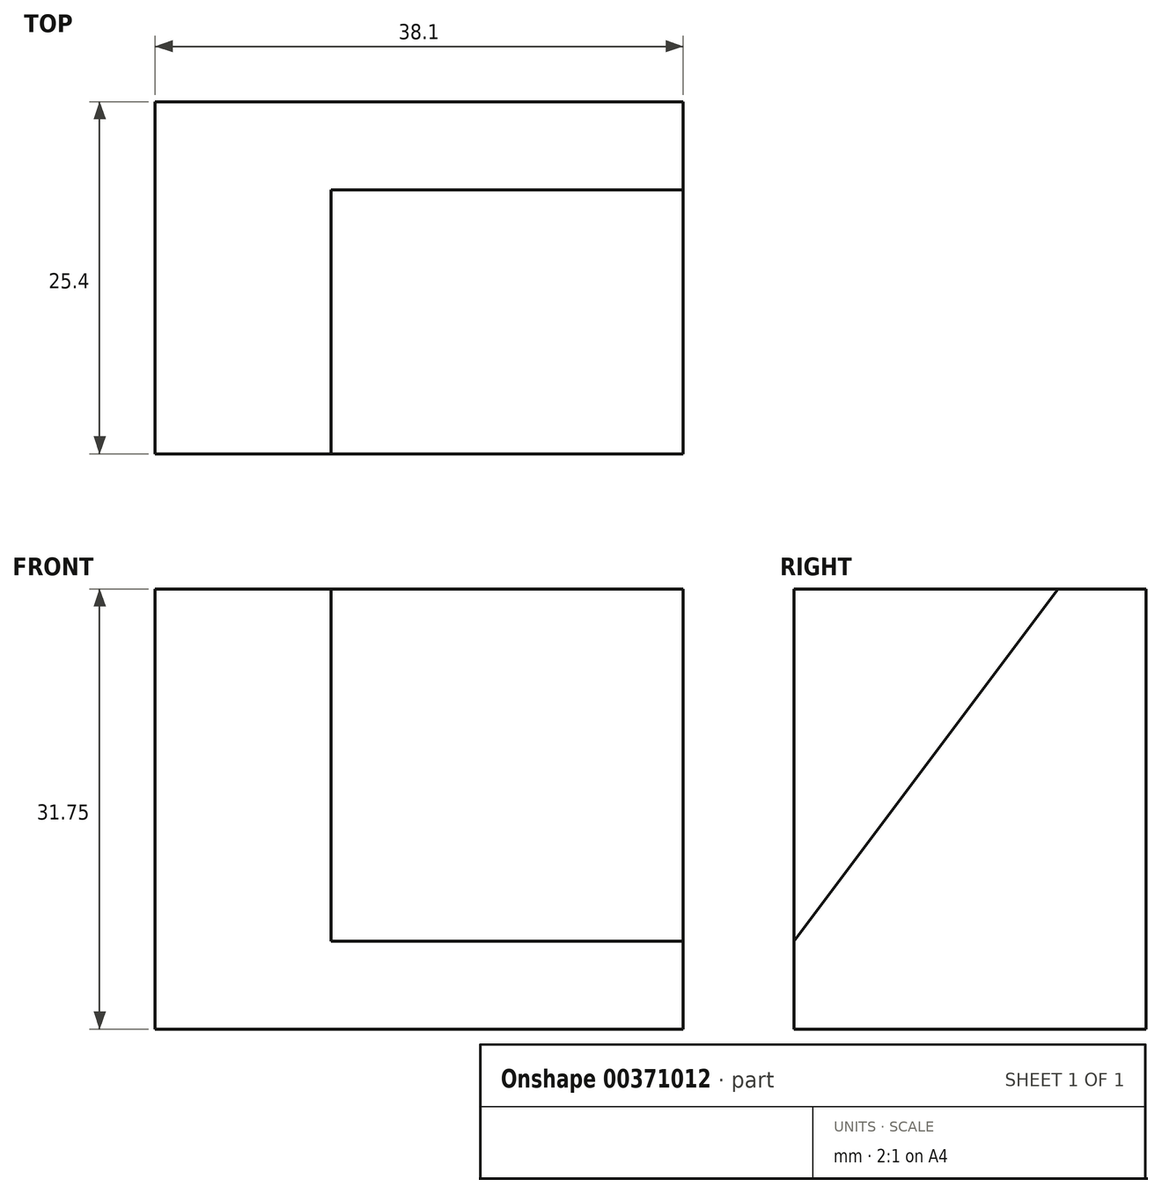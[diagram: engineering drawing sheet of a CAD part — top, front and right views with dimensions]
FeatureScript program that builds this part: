
annotation { "Feature Type Name" : "Feature", "Feature Type Description" : "" }
export const myFeature = defineFeature(function(context is Context, id is Id, definition is map)
    precondition{}
    {
        {
            var Q0;
            Q0=qCreatedBy(makeId("Top.planeOp"),FACE);
            var sketch = newSketch(context, id + "F0", { "sketchPlane" : qUnion([Q0])});
            skLineSegment(sketch, "E0", {"start": v(0, 0) * mm, "end": v(38.1, 0) * mm});
            skLineSegment(sketch, "E1", {"start": v(38.1, 0) * mm, "end": v(38.1, 25.4) * mm});
            skLineSegment(sketch, "E2", {"start": v(38.1, 25.4) * mm, "end": v(0, 25.4) * mm});
            skLineSegment(sketch, "E3", {"start": v(0, 25.4) * mm, "end": v(0, 0) * mm});
            skSolve(sketch);
        }
        {
            var Q0;
            Q0=makeQuery(id+"F0.imprint","IMPRINT",FACE,{"disambiguationData":[TD([[makeQuery(id+"F0.imprint","IMPRINT",EDGE,{"derivedFrom":sQuery(id+"F0.wireOp",EDGE,"E0")}),1.0]])]});
            extrude(context, id + "F1", {"entities" : qUnion([Q0]), "depth" : 31.75 * mm});
        }
        {
            var Q0;
            Q0=makeQuery(id+"F1.opExtrude","SWEPT_FACE",FACE,{"disambiguationData":[OSD([sQuery(id+"F0.wireOp",EDGE,"E1")])]});
            var sketch = newSketch(context, id + "F2", { "sketchPlane" : qUnion([Q0])});
            skLineSegment(sketch, "E4", {"start": v(0, 31.75) * mm, "end": v(19.05, 31.75) * mm});
            skLineSegment(sketch, "E5", {"start": v(19.05, 31.75) * mm, "end": v(0, 6.35) * mm});
            skLineSegment(sketch, "E6", {"start": v(0, 6.35) * mm, "end": v(0, 31.75) * mm});
            skSolve(sketch);
        }
        {
            var Q0;
            Q0 = qSketchRegion(id + "F2", true);
            extrude(context, id + "F3", {"entities" : qUnion([Q0]), "operationType" : NewBodyOperationType.REMOVE, "oppositeDirection" : true, "depth" : 25.4 * mm});
        }
    });
